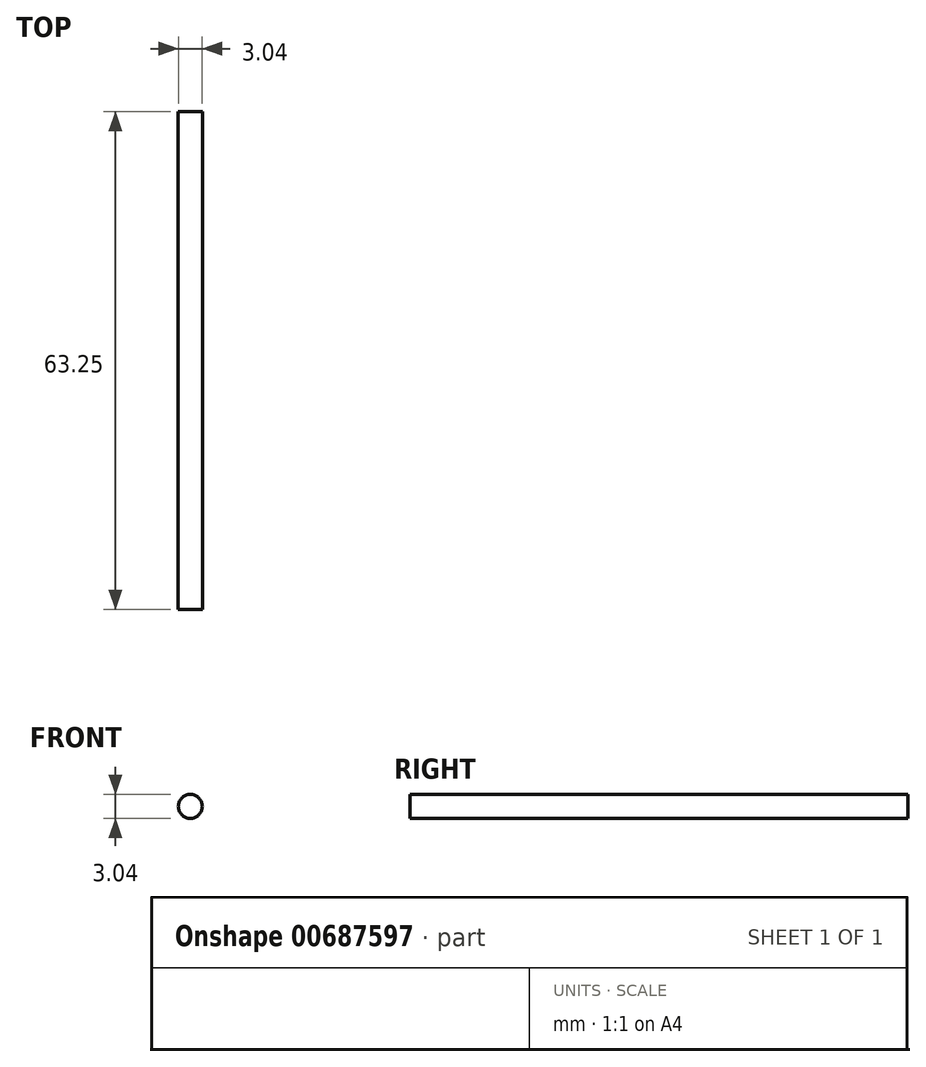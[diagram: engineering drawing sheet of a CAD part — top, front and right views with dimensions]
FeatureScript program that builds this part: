
annotation { "Feature Type Name" : "Feature", "Feature Type Description" : "" }
export const myFeature = defineFeature(function(context is Context, id is Id, definition is map)
    precondition{}
    {
        {
            var Q0;
            Q0=qCreatedBy(makeId("Front.planeOp"),FACE);
            var sketch = newSketch(context, id + "F0", { "sketchPlane" : qUnion([Q0])});
            skCircle(sketch, "E0", {"center": v(0, 0) * mm, "radius": 1.52 * mm});
            skSolve(sketch);
        }
        {
            var Q0;
            Q0=makeQuery(id+"F0.imprint","IMPRINT",FACE,{"disambiguationData":[TD([[makeQuery(id+"F0.imprint","IMPRINT",EDGE,{"derivedFrom":sQuery(id+"F0.wireOp",EDGE,"E0")}),1.0]])]});
            extrude(context, id + "F1", {"entities" : qUnion([Q0]), "depth" : 63.25 * mm, "offsetDistance" : 25.4 * mm});
        }
    });
